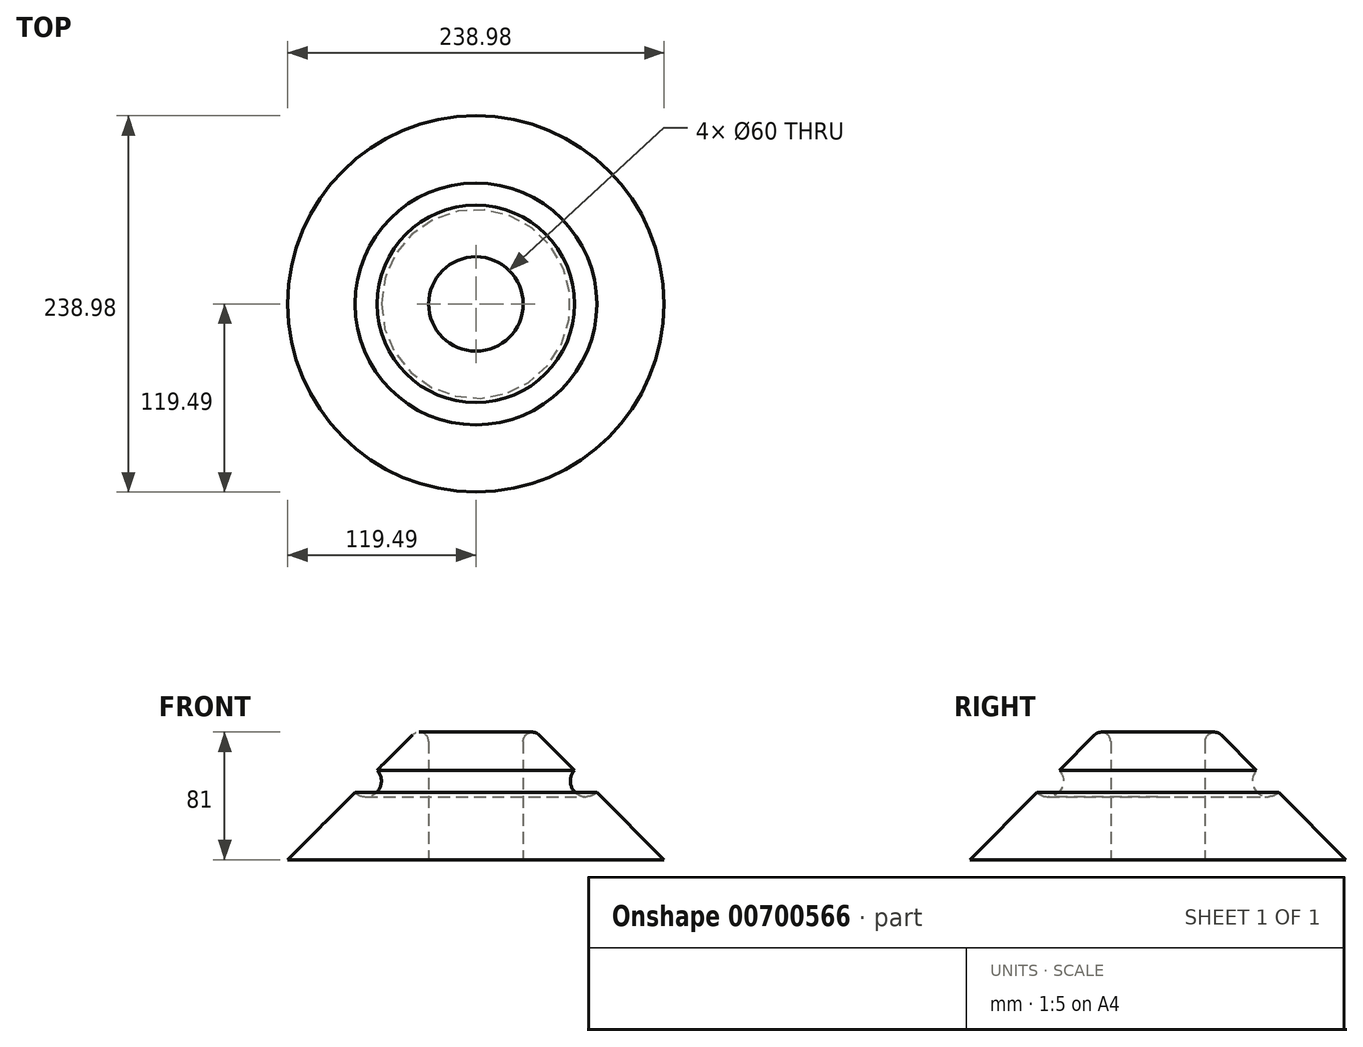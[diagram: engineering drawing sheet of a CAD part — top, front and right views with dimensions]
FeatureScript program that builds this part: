
annotation { "Feature Type Name" : "Feature", "Feature Type Description" : "" }
export const myFeature = defineFeature(function(context is Context, id is Id, definition is map)
    precondition{}
    {
        {
            var Q0;
            Q0=qCreatedBy(makeId("Front.planeOp"),FACE);
            var sketch = newSketch(context, id + "F0", { "sketchPlane" : qUnion([Q0])});
            skLineSegment(sketch, "E0", {"start": v(-30, 0) * mm, "end": v(-30, 75) * mm});
            skLineSegment(sketch, "E1", {"start": v(-40.24, 79.24) * mm, "end": v(-119.49, 0) * mm});
            skLineSegment(sketch, "E2", {"start": v(-119.49, 0) * mm, "end": v(-30, 0) * mm});
            skPoint(sketch, "E3.visualSharp", {"position": v(-30, 89.49) * mm});
            skArc(sketch, "E3.filletArc", {"start": v(-30, 75) * mm, "mid": v(-33.7, 80.54) * mm, "end": v(-40.24, 79.24) * mm});
            skLineSegment(sketch, "E4", {"start": v(0, 0) * mm, "end": v(0, 102.65) * mm, "construction": true});
            skSolve(sketch);
        }
        {
            var Q0;
            Q0=makeQuery(id+"F0.imprint","IMPRINT",FACE,{"disambiguationData":[TD([[makeQuery(id+"F0.imprint","IMPRINT",EDGE,{"derivedFrom":sQuery(id+"F0.wireOp",EDGE,"E0")}),1.0]])]});
            var Q1;
            Q1=sQuery(id+"F0.wireOp",EDGE,"E4");
            revolve(context, id + "F1", {"entities" : qUnion([Q0]), "axis" : qUnion([Q1]), "revolveType" : RevolveType.FULL});
        }
        {
            var Q0;
            Q0=qCreatedBy(makeId("Front.planeOp"),FACE);
            var sketch = newSketch(context, id + "F2", { "sketchPlane" : qUnion([Q0])});
            skCircle(sketch, "E5", {"center": v(-70, 50) * mm, "radius": 10 * mm});
            skLineSegment(sketch, "E6", {"start": v(0, 0) * mm, "end": v(0, 120.93) * mm, "construction": true});
            skSolve(sketch);
        }
        {
            var Q0;
            Q0=makeQuery(id+"F2.imprint","IMPRINT",FACE,{"disambiguationData":[TD([[makeQuery(id+"F2.imprint","IMPRINT",EDGE,{"derivedFrom":sQuery(id+"F2.wireOp",EDGE,"E5")}),1.0]])]});
            var Q1;
            Q1=sQuery(id+"F2.wireOp",EDGE,"E6");
            revolve(context, id + "F3", {"operationType" : NewBodyOperationType.REMOVE, "entities" : qUnion([Q0]), "axis" : qUnion([Q1]), "revolveType" : RevolveType.FULL});
        }
    });
